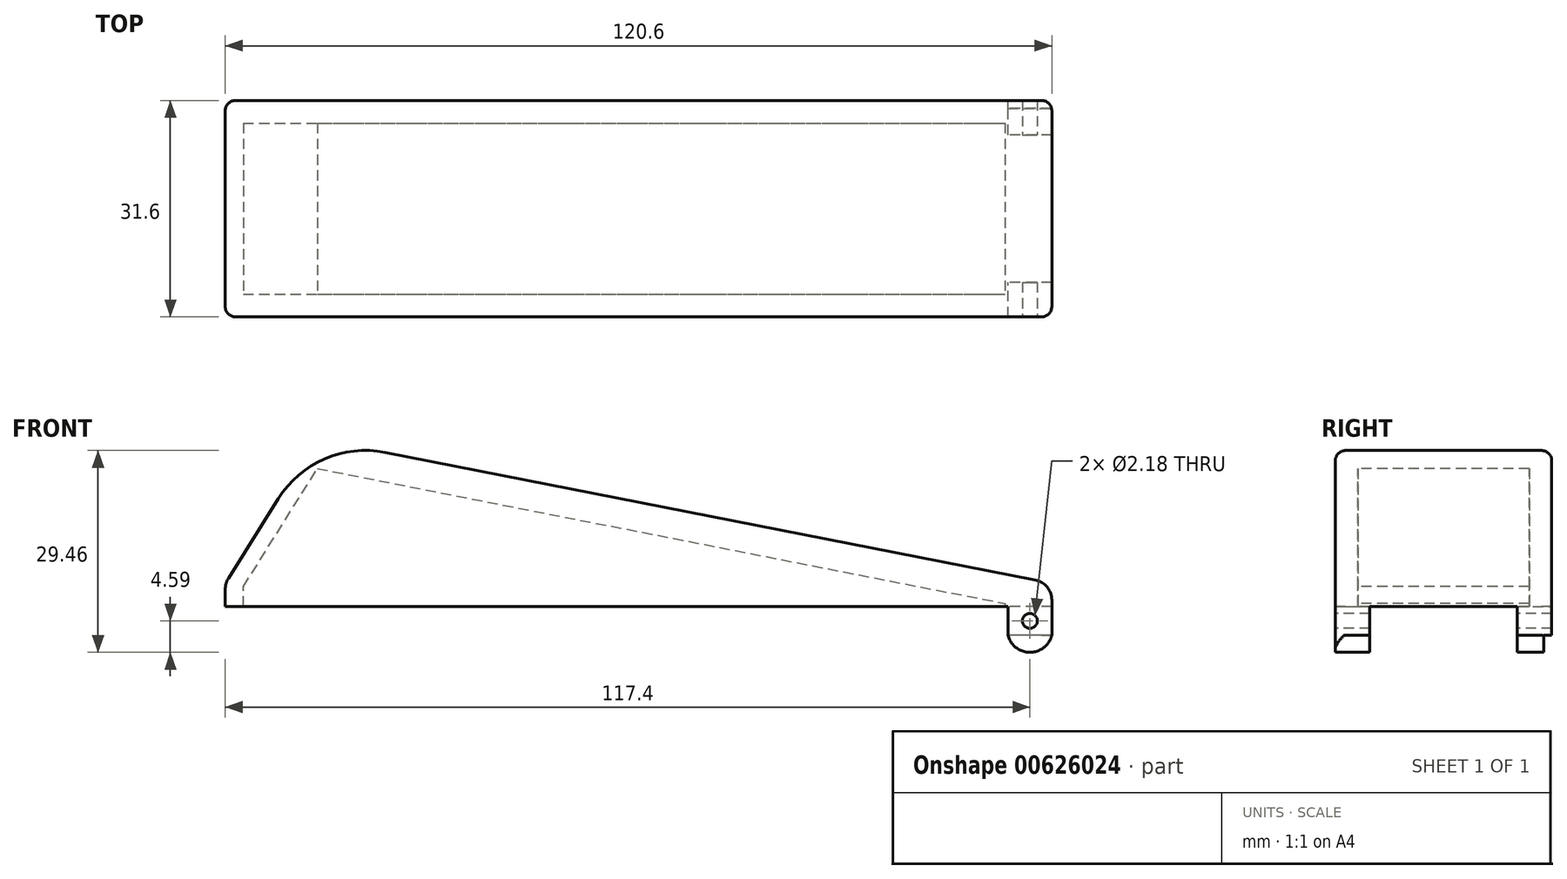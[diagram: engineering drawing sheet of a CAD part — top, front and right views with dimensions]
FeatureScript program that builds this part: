
annotation { "Feature Type Name" : "Feature", "Feature Type Description" : "" }
export const myFeature = defineFeature(function(context is Context, id is Id, definition is map)
    precondition{}
    {
        {
            var Q0;
            Q0=qCreatedBy(makeId("Front.planeOp"),FACE);
            var sketch = newSketch(context, id + "F0", { "sketchPlane" : qUnion([Q0])});
            skLineSegment(sketch, "E0", {"start": v(-60.3, 0) * mm, "end": v(60.3, 0) * mm});
            skLineSegment(sketch, "E1", {"start": v(60.3, 0) * mm, "end": v(60.3, 3.4) * mm});
            skLineSegment(sketch, "E2", {"start": v(-60.3, 0) * mm, "end": v(-60.3, 3.4) * mm});
            skLineSegment(sketch, "E3", {"start": v(-60.3, 3.4) * mm, "end": v(-47.08, 24.47) * mm});
            skLineSegment(sketch, "E4", {"start": v(-47.08, 24.47) * mm, "end": v(60.3, 3.4) * mm});
            skLineSegment(sketch, "E5", {"start": v(60.3, 0) * mm, "end": v(60.3, -4.2) * mm});
            skLineSegment(sketch, "E6", {"start": v(60.3, -4.2) * mm, "end": v(53.9, -4.2) * mm});
            skLineSegment(sketch, "E7", {"start": v(53.9, -4.2) * mm, "end": v(53.9, 0) * mm});
            skPoint(sketch, "E8", {"position": v(0, 0) * mm});
            skSolve(sketch);
        }
        {
            var Q0;
            Q0 = qSketchRegion(id + "F0", true);
            var Q1;
            {var subQ1=sQuery(id+"F0.wireOp",EDGE,"E1");Q1=makeQuery(id+"F0.imprint","IMPRINT",FACE,{"disambiguationData":[TD([[makeQuery(id+"F0.imprint","IMPRINT",EDGE,{"derivedFrom":subQ1}),1.0]])]});}
            extrude(context, id + "F1", {"entities" : qUnion([Q0, Q1]), "depth" : 31.6 * mm, "offsetDistance" : 25 * mm, "symmetric" : true});
        }
        {
            var Q0;
            Q0=makeQuery(id+"F1.opExtrude","SWEPT_EDGE",EDGE,{"disambiguationData":[OSD([sQuery(id+"F0.wireOp",EDGE,"E3"),sQuery(id+"F0.wireOp",EDGE,"E4")])]});
            fillet(context, id + "F2", {"entities" : qUnion([Q0]), "radius" : 15 * mm, "tangentPropagation" : true, "allowEdgeOverflow" : false});
        }
        {
            var Q0;
            Q0=makeQuery(id+"F1.opExtrude","SWEPT_EDGE",EDGE,{"disambiguationData":[OSD([sQuery(id+"F0.wireOp",EDGE,"E2"),sQuery(id+"F0.wireOp",EDGE,"E3")])]});
            var Q1;
            Q1=makeQuery(id+"F1.opExtrude","SWEPT_EDGE",EDGE,{"disambiguationData":[OSD([sQuery(id+"F0.wireOp",EDGE,"E1"),sQuery(id+"F0.wireOp",EDGE,"E4")])]});
            fillet(context, id + "F3", {"entities" : qUnion([Q0, Q1]), "radius" : 3 * mm, "tangentPropagation" : true, "allowEdgeOverflow" : false});
        }
        {
            var Q0;
            Q0=makeQuery(id+"F1.opExtrude","SWEPT_FACE",FACE,{"disambiguationData":[OSD([sQuery(id+"F0.wireOp",EDGE,"E6")])]});
            var sketch = newSketch(context, id + "F4", { "sketchPlane" : qUnion([Q0])});
            skLineSegment(sketch, "E9", {"start": v(60.3, 10.76) * mm, "end": v(53.9, 10.76) * mm});
            skLineSegment(sketch, "E10", {"start": v(60.3, -10.76) * mm, "end": v(53.9, -10.76) * mm});
            skLineSegment(sketch, "E11", {"start": v(60.3, 10.76) * mm, "end": v(60.3, -10.76) * mm});
            skLineSegment(sketch, "E12", {"start": v(53.9, -10.76) * mm, "end": v(53.9, 10.76) * mm});
            skSolve(sketch);
        }
        {
            var Q0;
            Q0=makeQuery(id+"F4.imprint","IMPRINT",FACE,{"disambiguationData":[TD([[makeQuery(id+"F4.imprint","IMPRINT",EDGE,{"derivedFrom":sQuery(id+"F4.wireOp",EDGE,"E9")}),1.0]])]});
            extrude(context, id + "F5", {"entities" : qUnion([Q0]), "operationType" : NewBodyOperationType.REMOVE, "oppositeDirection" : true, "depth" : 4.2 * mm, "offsetDistance" : 25 * mm});
        }
        {
            var Q0;
            Q0=makeQuery(id+"F1.opExtrude","CAP_FACE",FACE,{"disambiguationData":[OSD([sQuery(id+"F0.wireOp",EDGE,"E0"),sQuery(id+"F0.wireOp",EDGE,"E1"),sQuery(id+"F0.wireOp",EDGE,"E2"),sQuery(id+"F0.wireOp",EDGE,"E3"),sQuery(id+"F0.wireOp",EDGE,"E4"),sQuery(id+"F0.wireOp",EDGE,"E5"),sQuery(id+"F0.wireOp",EDGE,"E6"),sQuery(id+"F0.wireOp",EDGE,"E7")])],"isStart":false});
            var sketch = newSketch(context, id + "F6", { "sketchPlane" : qUnion([Q0])});
            skCircle(sketch, "E13", {"center": v(57.1, -2.1) * mm, "radius": 1.09 * mm});
            skPoint(sketch, "E13.centerSnap0", {"position": v(53.9, -2.1) * mm});
            skPoint(sketch, "E13.centerSnap1", {"position": v(57.1, -4.2) * mm});
            skSolve(sketch);
        }
        {
            var Q0;
            Q0=makeQuery(id+"F6.imprint","IMPRINT",FACE,{"disambiguationData":[TD([[makeQuery(id+"F6.imprint","IMPRINT",EDGE,{"derivedFrom":sQuery(id+"F6.wireOp",EDGE,"E13")}),1.0]])]});
            extrude(context, id + "F7", {"entities" : qUnion([Q0]), "operationType" : NewBodyOperationType.REMOVE, "endBound" : BoundingType.THROUGH_ALL, "oppositeDirection" : true, "depth" : 25 * mm, "offsetDistance" : 25 * mm});
        }
        {
            var Q0;
            Q0=makeQuery(id+"F1.opExtrude","CAP_FACE",FACE,{"disambiguationData":[OSD([sQuery(id+"F0.wireOp",EDGE,"E0"),sQuery(id+"F0.wireOp",EDGE,"E1"),sQuery(id+"F0.wireOp",EDGE,"E2"),sQuery(id+"F0.wireOp",EDGE,"E3"),sQuery(id+"F0.wireOp",EDGE,"E4"),sQuery(id+"F0.wireOp",EDGE,"E5"),sQuery(id+"F0.wireOp",EDGE,"E6"),sQuery(id+"F0.wireOp",EDGE,"E7")])],"isStart":false});
            var sketch = newSketch(context, id + "F8", { "sketchPlane" : qUnion([Q0])});
            skArc(sketch, "E14", {"start": v(53.9, -4.2) * mm, "mid": v(57.1, -6.7) * mm, "end": v(60.3, -4.2) * mm});
            skSolve(sketch);
        }
        {
            var Q0;
            Q0 = qSketchRegion(id + "F8", true);
            var Q1;
            Q1=makeQuery(id+"F8.imprint","IMPRINT",FACE,{"disambiguationData":[TD([[makeQuery(id+"F8.imprint","IMPRINT",EDGE,{"derivedFrom":sQuery(id+"F8.wireOp",EDGE,"E14")}),1.0]])]});
            extrude(context, id + "F9", {"entities" : qUnion([Q0, Q1]), "operationType" : NewBodyOperationType.ADD, "oppositeDirection" : true, "depth" : 30.4 * mm, "offsetDistance" : 25 * mm});
        }
        {
            var Q0;
            Q0=makeQuery(id+"F4.imprint","IMPRINT",FACE,{"disambiguationData":[TD([[makeQuery(id+"F4.imprint","IMPRINT",EDGE,{"derivedFrom":sQuery(id+"F4.wireOp",EDGE,"E9")}),1.0]])]});
            extrude(context, id + "F10", {"entities" : qUnion([Q0]), "operationType" : NewBodyOperationType.REMOVE, "depth" : 25 * mm, "offsetDistance" : 25 * mm});
        }
        {
            var Q0;
            Q0=makeQuery(id+"F1.opExtrude","CAP_EDGE",EDGE,{"disambiguationData":[OSD([sQuery(id+"F0.wireOp",EDGE,"E3")])],"isStart":false});
            var Q1;
            Q1=makeQuery(id+"F1.opExtrude","CAP_EDGE",EDGE,{"disambiguationData":[OSD([sQuery(id+"F0.wireOp",EDGE,"E4")])],"isStart":true});
            var Q2;
            Q2=qNothing();
            fillet(context, id + "F11", {"entities" : qUnion([Q0, Q1, Q2]), "radius" : 1.5 * mm, "tangentPropagation" : true, "allowEdgeOverflow" : false});
        }
        {
            var Q0;
            {var subQ1=sQuery(id+"F0.wireOp",EDGE,"E1");Q0=makeQuery(id+"F0.imprint","IMPRINT",FACE,{"disambiguationData":[TD([[makeQuery(id+"F0.imprint","IMPRINT",EDGE,{"derivedFrom":subQ1}),1.0]])]});}
            var sketch = newSketch(context, id + "F12", { "sketchPlane" : qUnion([Q0])});
            skLineSegment(sketch, "E15", {"start": v(-57.67, 0) * mm, "end": v(-57.67, 2.89) * mm});
            skLineSegment(sketch, "E16", {"start": v(-57.67, 2.89) * mm, "end": v(-46.86, 20.12) * mm});
            skLineSegment(sketch, "E17", {"start": v(-46.86, 20.12) * mm, "end": v(53.48, 0.43) * mm});
            skLineSegment(sketch, "E18", {"start": v(53.48, 0.43) * mm, "end": v(53.48, 0) * mm});
            skSolve(sketch);
        }
        {
            var Q0;
            {var subQ1=sQuery(id+"F12.wireOp",EDGE,"E15");Q0=makeQuery(id+"F12.imprint","IMPRINT",FACE,{"disambiguationData":[TD([[makeQuery(id+"F12.imprint","IMPRINT",EDGE,{"derivedFrom":subQ1}),-1.0]])]});}
            extrude(context, id + "F13", {"entities" : qUnion([Q0]), "operationType" : NewBodyOperationType.REMOVE, "oppositeDirection" : true, "depth" : 25 * mm, "offsetDistance" : 25 * mm, "symmetric" : true});
        }
    });
